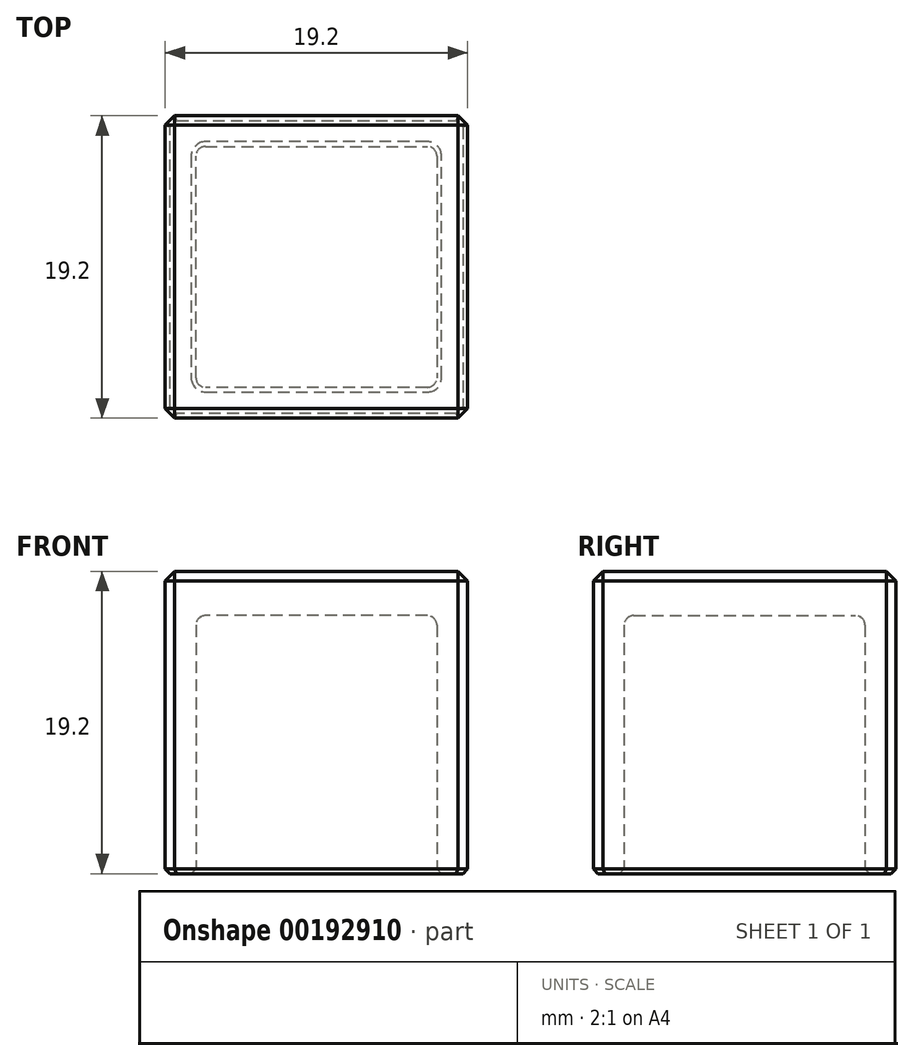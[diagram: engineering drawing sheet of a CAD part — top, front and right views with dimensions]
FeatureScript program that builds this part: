
annotation { "Feature Type Name" : "Feature", "Feature Type Description" : "" }
export const myFeature = defineFeature(function(context is Context, id is Id, definition is map)
    precondition{}
    {
        {
            var Q0;
            Q0=qCreatedBy(makeId("Top.planeOp"),FACE);
            var sketch = newSketch(context, id + "F0", { "sketchPlane" : qUnion([Q0])});
            skLineSegment(sketch, "E0.bottom", {"start": v(9.6, -9.6) * mm, "end": v(-9.6, -9.6) * mm});
            skLineSegment(sketch, "E0.top", {"start": v(9.6, 9.6) * mm, "end": v(-9.6, 9.6) * mm});
            skLineSegment(sketch, "E0.left", {"start": v(9.6, -9.6) * mm, "end": v(9.6, 9.6) * mm});
            skLineSegment(sketch, "E0.right", {"start": v(-9.6, -9.6) * mm, "end": v(-9.6, 9.6) * mm});
            skPoint(sketch, "E0.middle", {"position": v(0, 0) * mm});
            skSolve(sketch);
        }
        {
            var Q0;
            Q0 = qSketchRegion(id + "F0", true);
            extrude(context, id + "F1", {"entities" : qUnion([Q0]), "depth" : 19.2 * mm});
        }
        {
            var Q0;
            Q0=makeQuery(id+"F1.opExtrude","CAP_FACE",FACE,{"disambiguationData":[OSD([sQuery(id+"F0.wireOp",EDGE,"E0.bottom"),sQuery(id+"F0.wireOp",EDGE,"E0.top"),sQuery(id+"F0.wireOp",EDGE,"E0.left"),sQuery(id+"F0.wireOp",EDGE,"E0.right")])],"isStart":true});
            var sketch = newSketch(context, id + "F2", { "sketchPlane" : qUnion([Q0])});
            skLineSegment(sketch, "E1.bottom", {"start": v(7.65, 7.65) * mm, "end": v(-7.65, 7.65) * mm});
            skLineSegment(sketch, "E1.top", {"start": v(7.65, -7.65) * mm, "end": v(-7.65, -7.65) * mm});
            skLineSegment(sketch, "E1.left", {"start": v(7.65, 7.65) * mm, "end": v(7.65, -7.65) * mm});
            skLineSegment(sketch, "E1.right", {"start": v(-7.65, 7.65) * mm, "end": v(-7.65, -7.65) * mm});
            skPoint(sketch, "E1.middle", {"position": v(0, 0) * mm});
            skSolve(sketch);
        }
        {
            var Q0;
            Q0 = qSketchRegion(id + "F2", true);
            extrude(context, id + "F3", {"entities" : qUnion([Q0]), "operationType" : NewBodyOperationType.REMOVE, "oppositeDirection" : true, "depth" : 16.4 * mm});
        }
        {
            var Q0;
            Q0=makeQuery(id+"F1.opExtrude","SWEPT_EDGE",EDGE,{"disambiguationData":[OSD([sQuery(id+"F0.wireOp",EDGE,"E0.bottom"),sQuery(id+"F0.wireOp",EDGE,"E0.right")])]});
            var Q1;
            Q1=makeQuery(id+"F1.opExtrude","SWEPT_EDGE",EDGE,{"disambiguationData":[OSD([sQuery(id+"F0.wireOp",EDGE,"E0.top"),sQuery(id+"F0.wireOp",EDGE,"E0.right")])]});
            var Q2;
            Q2=makeQuery(id+"F1.opExtrude","SWEPT_EDGE",EDGE,{"disambiguationData":[OSD([sQuery(id+"F0.wireOp",EDGE,"E0.top"),sQuery(id+"F0.wireOp",EDGE,"E0.left")])]});
            var Q3;
            Q3=makeQuery(id+"F1.opExtrude","SWEPT_EDGE",EDGE,{"disambiguationData":[OSD([sQuery(id+"F0.wireOp",EDGE,"E0.bottom"),sQuery(id+"F0.wireOp",EDGE,"E0.left")])]});
            var Q4;
            Q4=makeQuery(id+"F1.opExtrude","CAP_FACE",FACE,{"disambiguationData":[OSD([sQuery(id+"F0.wireOp",EDGE,"E0.bottom"),sQuery(id+"F0.wireOp",EDGE,"E0.top"),sQuery(id+"F0.wireOp",EDGE,"E0.left"),sQuery(id+"F0.wireOp",EDGE,"E0.right")])],"isStart":false});
            chamfer(context, id + "F4", {"entities" : qUnion([Q0, Q1, Q2, Q3, Q4]), "width" : 0.6 * mm, "tangentPropagation" : true});
        }
        {
            var Q0;
            Q0=makeQuery(id+"F3.boolean.opBoolean","COPY",EDGE,{"derivedFrom":makeQuery(id+"F3.opExtrude","SWEPT_EDGE",EDGE,{"disambiguationData":[OSD([sQuery(id+"F2.wireOp",EDGE,"E1.top"),sQuery(id+"F2.wireOp",EDGE,"E1.right")])]})});
            var Q1;
            Q1=makeQuery(id+"F3.boolean.opBoolean","COPY",EDGE,{"derivedFrom":makeQuery(id+"F3.opExtrude","SWEPT_EDGE",EDGE,{"disambiguationData":[OSD([sQuery(id+"F2.wireOp",EDGE,"E1.bottom"),sQuery(id+"F2.wireOp",EDGE,"E1.right")])]})});
            var Q2;
            Q2=makeQuery(id+"F3.boolean.opBoolean","COPY",EDGE,{"derivedFrom":makeQuery(id+"F3.opExtrude","SWEPT_EDGE",EDGE,{"disambiguationData":[OSD([sQuery(id+"F2.wireOp",EDGE,"E1.bottom"),sQuery(id+"F2.wireOp",EDGE,"E1.left")])]})});
            var Q3;
            Q3=makeQuery(id+"F3.boolean.opBoolean","COPY",EDGE,{"derivedFrom":makeQuery(id+"F3.opExtrude","SWEPT_EDGE",EDGE,{"disambiguationData":[OSD([sQuery(id+"F2.wireOp",EDGE,"E1.top"),sQuery(id+"F2.wireOp",EDGE,"E1.left")])]})});
            var Q4;
            Q4=makeQuery(id+"F3.boolean.opBoolean","COPY",FACE,{"derivedFrom":makeQuery(id+"F3.opExtrude","CAP_FACE",FACE,{"disambiguationData":[OSD([sQuery(id+"F2.wireOp",EDGE,"E1.bottom"),sQuery(id+"F2.wireOp",EDGE,"E1.top"),sQuery(id+"F2.wireOp",EDGE,"E1.left"),sQuery(id+"F2.wireOp",EDGE,"E1.right")])],"isStart":false})});
            fillet(context, id + "F5", {"entities" : qUnion([Q0, Q1, Q2, Q3, Q4]), "radius" : 0.6 * mm, "tangentPropagation" : true, "allowEdgeOverflow" : false});
        }
        {
            var Q0;
            Q0=makeQuery(id+"F1.opExtrude","CAP_FACE",FACE,{"disambiguationData":[OSD([sQuery(id+"F0.wireOp",EDGE,"E0.bottom"),sQuery(id+"F0.wireOp",EDGE,"E0.top"),sQuery(id+"F0.wireOp",EDGE,"E0.left"),sQuery(id+"F0.wireOp",EDGE,"E0.right")])],"isStart":true});
            chamfer(context, id + "F6", {"entities" : qUnion([Q0]), "width" : 0.3 * mm, "tangentPropagation" : true});
        }
    });
